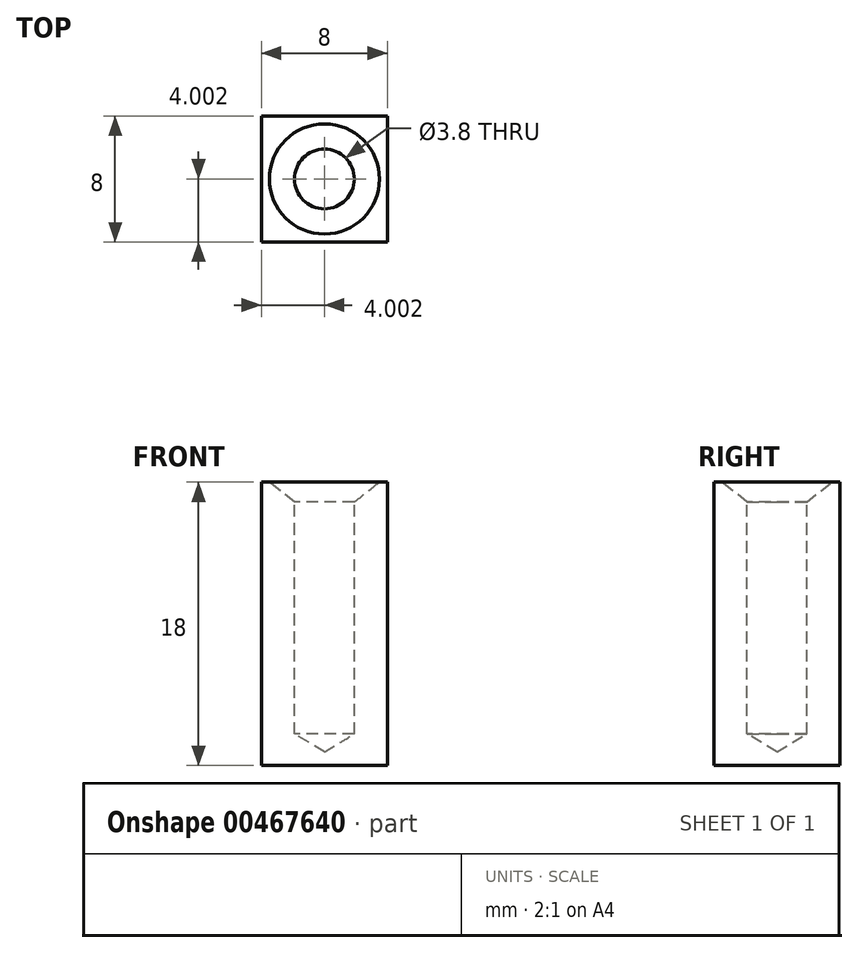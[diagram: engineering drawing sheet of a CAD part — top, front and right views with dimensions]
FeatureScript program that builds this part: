
annotation { "Feature Type Name" : "Feature", "Feature Type Description" : "" }
export const myFeature = defineFeature(function(context is Context, id is Id, definition is map)
    precondition{}
    {
        {
            var Q0;
            Q0=qCreatedBy(makeId("Top.planeOp"),FACE);
            var sketch = newSketch(context, id + "F0", { "sketchPlane" : qUnion([Q0])});
            skLineSegment(sketch, "E0.bottom", {"start": v(-42.95, 29.1) * mm, "end": v(-34.95, 29.1) * mm});
            skLineSegment(sketch, "E0.top", {"start": v(-42.95, 21.1) * mm, "end": v(-34.95, 21.1) * mm});
            skLineSegment(sketch, "E0.left", {"start": v(-42.95, 29.1) * mm, "end": v(-42.95, 21.1) * mm});
            skLineSegment(sketch, "E0.right", {"start": v(-34.95, 29.1) * mm, "end": v(-34.95, 21.1) * mm});
            skLineSegment(sketch, "E1", {"start": v(-42.95, 29.1) * mm, "end": v(-34.95, 21.1) * mm, "construction": true});
            skLineSegment(sketch, "E2", {"start": v(-42.95, 21.1) * mm, "end": v(-34.95, 29.1) * mm, "construction": true});
            skSolve(sketch);
        }
        {
            var Q0;
            Q0=qCreatedBy(makeId("Top.planeOp"),FACE);
            var sketch = newSketch(context, id + "F1", { "sketchPlane" : qUnion([Q0])});
            skCircle(sketch, "E3", {"center": v(-38.95, 25.1) * mm, "radius": 1.95 * mm});
            skSolve(sketch);
        }
        {
            var Q0;
            Q0 = qSketchRegion(id + "F0", true);
            extrude(context, id + "F2", {"entities" : qUnion([Q0]), "oppositeDirection" : true, "depth" : 18 * mm});
        }
        {
            var Q0;
            Q0=sQuery(id+"F1.wireOp",VERTEX,"E3.center");
            var Q1;
            Q1=makeQuery(id+"F2.opExtrude","SWEPT_BODY",BODY,{"disambiguationData":[OSD([sQuery(id+"F0.wireOp",EDGE,"E0.bottom"),sQuery(id+"F0.wireOp",EDGE,"E0.top"),sQuery(id+"F0.wireOp",EDGE,"E0.left"),sQuery(id+"F0.wireOp",EDGE,"E0.right")])]});
            hole(context, id + "F3", {"style" : HoleStyle.C_SINK, "endStyle" : HoleEndStyle.BLIND, "holeDiameter" : 3.8 * mm, "cSinkDiameter" : 7 * mm, "cSinkAngle" : 1.8 * radian, "holeDepth" : 16 * mm, "isTappedThrough" : true, "tappedDepth" : 12 * mm, "tapClearance" : 3, "locations" : qUnion([Q0]), "scope" : qUnion([Q1])});
        }
    });
